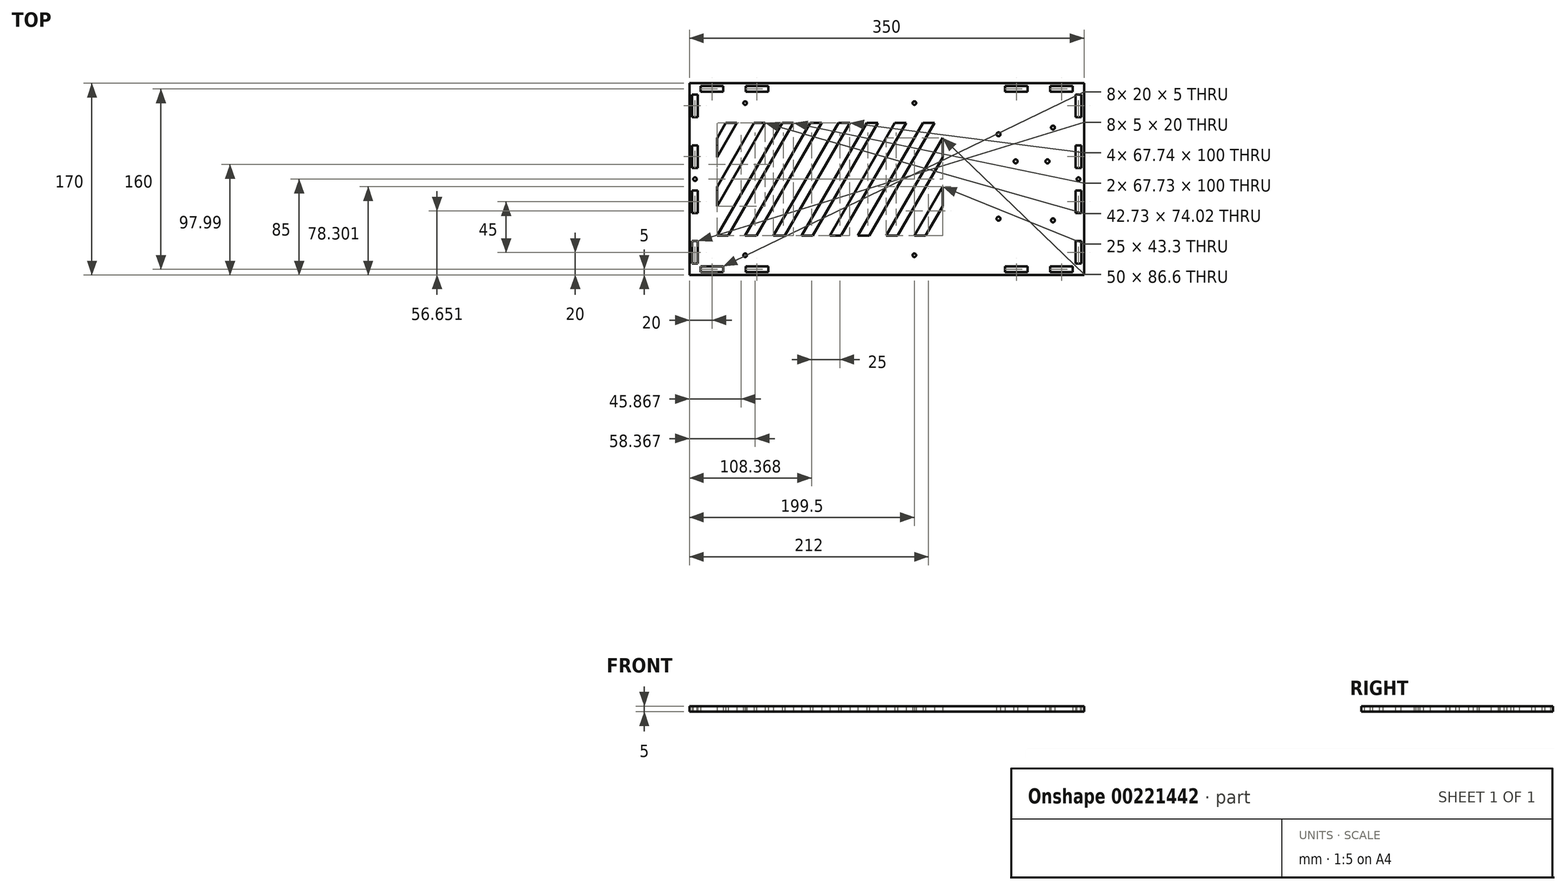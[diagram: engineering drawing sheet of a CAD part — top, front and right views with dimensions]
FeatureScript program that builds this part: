
annotation { "Feature Type Name" : "Feature", "Feature Type Description" : "" }
export const myFeature = defineFeature(function(context is Context, id is Id, definition is map)
    precondition{}
    {
        {
            assignVariable(context, id + "F0", {"name" : "thickness", "anyValue" : 5 * mm});
        }
        {
            var Q0;
            Q0=qCreatedBy(makeId("Top.planeOp"),FACE);
            var sketch = newSketch(context, id + "F1", { "sketchPlane" : qUnion([Q0])});
            skLineSegment(sketch, "E0.bottom", {"start": v(0, 0) * mm, "end": v(350, 0) * mm});
            skLineSegment(sketch, "E0.top", {"start": v(0, 170) * mm, "end": v(350, 170) * mm});
            skLineSegment(sketch, "E0.left", {"start": v(0, 0) * mm, "end": v(0, 170) * mm});
            skLineSegment(sketch, "E0.right", {"start": v(350, 0) * mm, "end": v(350, 170) * mm});
            skLineSegment(sketch, "E1.0", {"start": v(10, 160) * mm, "end": v(340, 160) * mm, "construction": true});
            skLineSegment(sketch, "E1.1", {"start": v(10, 10) * mm, "end": v(10, 160) * mm, "construction": true});
            skLineSegment(sketch, "E1.2", {"start": v(10, 10) * mm, "end": v(340, 10) * mm, "construction": true});
            skLineSegment(sketch, "E1.3", {"start": v(340, 10) * mm, "end": v(340, 160) * mm, "construction": true});
            skLineSegment(sketch, "E2.bottom", {"start": v(325, 34.25) * mm, "end": v(325, 135.75) * mm, "construction": true});
            skLineSegment(sketch, "E2.top", {"start": v(271.5, 34.25) * mm, "end": v(271.5, 135.75) * mm, "construction": true});
            skLineSegment(sketch, "E2.left", {"start": v(325, 34.25) * mm, "end": v(271.5, 34.25) * mm, "construction": true});
            skLineSegment(sketch, "E2.right", {"start": v(325, 135.75) * mm, "end": v(271.5, 135.75) * mm, "construction": true});
            skCircle(sketch, "E3", {"center": v(322.4, 48.45) * mm, "radius": 1.75 * mm});
            skCircle(sketch, "E4", {"center": v(274.1, 49.85) * mm, "radius": 1.75 * mm});
            skCircle(sketch, "E5", {"center": v(289.3, 100.75) * mm, "radius": 1.75 * mm});
            skCircle(sketch, "E6", {"center": v(317.5, 100.75) * mm, "radius": 1.75 * mm});
            skCircle(sketch, "E7", {"center": v(274.1, 124.75) * mm, "radius": 1.75 * mm});
            skCircle(sketch, "E8", {"center": v(322.4, 130.75) * mm, "radius": 1.75 * mm});
            skPoint(sketch, "E9", {"position": v(298.25, 34.25) * mm});
            skPoint(sketch, "E10", {"position": v(325, 85) * mm});
            skPoint(sketch, "E11", {"position": v(340, 85) * mm});
            skLineSegment(sketch, "E12.bottom", {"start": v(17, 142.5) * mm, "end": v(232, 142.5) * mm, "construction": true});
            skLineSegment(sketch, "E12.top", {"start": v(17, 27.5) * mm, "end": v(232, 27.5) * mm, "construction": true});
            skLineSegment(sketch, "E12.left", {"start": v(17, 142.5) * mm, "end": v(17, 27.5) * mm, "construction": true});
            skLineSegment(sketch, "E12.right", {"start": v(232, 142.5) * mm, "end": v(232, 27.5) * mm, "construction": true});
            skPoint(sketch, "E13", {"position": v(232, 85) * mm});
            skCircle(sketch, "E14", {"center": v(199.5, 152.5) * mm, "radius": 1.6 * mm});
            skCircle(sketch, "E15", {"center": v(199.5, 17.5) * mm, "radius": 1.6 * mm});
            skLineSegment(sketch, "E16", {"start": v(199.5, 152.5) * mm, "end": v(199.5, 17.5) * mm, "construction": true});
            skPoint(sketch, "E17", {"position": v(199.5, 85) * mm});
            skCircle(sketch, "E18", {"center": v(49.5, 152.5) * mm, "radius": 1.6 * mm});
            skCircle(sketch, "E19", {"center": v(49.5, 17.5) * mm, "radius": 1.6 * mm});
            skLineSegment(sketch, "E20", {"start": v(49.5, 152.5) * mm, "end": v(49.5, 17.5) * mm, "construction": true});
            skPoint(sketch, "E21", {"position": v(49.5, 85) * mm});
            skLineSegment(sketch, "E22.bottom", {"start": v(10, 7.5) * mm, "end": v(30, 7.5) * mm});
            skLineSegment(sketch, "E22.top", {"start": v(10, 2.5) * mm, "end": v(30, 2.5) * mm});
            skLineSegment(sketch, "E22.left", {"start": v(10, 7.5) * mm, "end": v(10, 2.5) * mm});
            skLineSegment(sketch, "E22.right", {"start": v(30, 7.5) * mm, "end": v(30, 2.5) * mm});
            skPoint(sketch, "E22.middle", {"position": v(20, 5) * mm});
            skLineSegment(sketch, "E23", {"start": v(10, 10) * mm, "end": v(10, 0) * mm, "construction": true});
            skPoint(sketch, "E24", {"position": v(10, 5) * mm});
            skLineSegment(sketch, "E25.bottom", {"start": v(50, 7.5) * mm, "end": v(70, 7.5) * mm});
            skLineSegment(sketch, "E25.top", {"start": v(50, 2.5) * mm, "end": v(70, 2.5) * mm});
            skLineSegment(sketch, "E25.left", {"start": v(50, 7.5) * mm, "end": v(50, 2.5) * mm});
            skLineSegment(sketch, "E25.right", {"start": v(70, 7.5) * mm, "end": v(70, 2.5) * mm});
            skPoint(sketch, "E25.middle", {"position": v(60, 5) * mm});
            skLineSegment(sketch, "E26", {"start": v(175, 10) * mm, "end": v(175, 0) * mm, "construction": true});
            skLineSegment(sketch, "E27.MirrorCS", {"start": v(300, 2.5) * mm, "end": v(280, 2.5) * mm});
            skLineSegment(sketch, "E28.MirrorCS", {"start": v(320, 7.5) * mm, "end": v(320, 2.5) * mm});
            skPoint(sketch, "E29.MirrorP", {"position": v(330, 5) * mm});
            skLineSegment(sketch, "E30.MirrorCS", {"start": v(300, 7.5) * mm, "end": v(280, 7.5) * mm});
            skLineSegment(sketch, "E31.MirrorCS", {"start": v(340, 2.5) * mm, "end": v(320, 2.5) * mm});
            skLineSegment(sketch, "E32.MirrorCS", {"start": v(280, 7.5) * mm, "end": v(280, 2.5) * mm});
            skPoint(sketch, "E33.MirrorP", {"position": v(290, 5) * mm});
            skLineSegment(sketch, "E34.MirrorCS", {"start": v(300, 7.5) * mm, "end": v(300, 2.5) * mm});
            skLineSegment(sketch, "E35.MirrorCS", {"start": v(340, 7.5) * mm, "end": v(340, 2.5) * mm});
            skLineSegment(sketch, "E36.MirrorCS", {"start": v(340, 7.5) * mm, "end": v(320, 7.5) * mm});
            skLineSegment(sketch, "E37", {"start": v(0, 85) * mm, "end": v(350, 85) * mm, "construction": true});
            skLineSegment(sketch, "E38.MirrorCS", {"start": v(30, 162.5) * mm, "end": v(30, 167.5) * mm});
            skPoint(sketch, "E39.MirrorP", {"position": v(20, 165) * mm});
            skLineSegment(sketch, "E40.MirrorCS", {"start": v(10, 167.5) * mm, "end": v(30, 167.5) * mm});
            skLineSegment(sketch, "E41.MirrorCS", {"start": v(10, 162.5) * mm, "end": v(10, 167.5) * mm});
            skPoint(sketch, "E42.MirrorP", {"position": v(10, 165) * mm});
            skLineSegment(sketch, "E43.MirrorCS", {"start": v(10, 162.5) * mm, "end": v(30, 162.5) * mm});
            skLineSegment(sketch, "E44.MirrorCS", {"start": v(50, 167.5) * mm, "end": v(70, 167.5) * mm});
            skLineSegment(sketch, "E45.MirrorCS", {"start": v(50, 162.5) * mm, "end": v(50, 167.5) * mm});
            skLineSegment(sketch, "E46.MirrorCS", {"start": v(50, 162.5) * mm, "end": v(70, 162.5) * mm});
            skPoint(sketch, "E47.MirrorP", {"position": v(60, 165) * mm});
            skLineSegment(sketch, "E48.MirrorCS", {"start": v(70, 162.5) * mm, "end": v(70, 167.5) * mm});
            skLineSegment(sketch, "E49.MirrorCS", {"start": v(300, 167.5) * mm, "end": v(280, 167.5) * mm});
            skLineSegment(sketch, "E50.MirrorCS", {"start": v(280, 162.5) * mm, "end": v(280, 167.5) * mm});
            skLineSegment(sketch, "E51.MirrorCS", {"start": v(340, 167.5) * mm, "end": v(320, 167.5) * mm});
            skPoint(sketch, "E52.MirrorP", {"position": v(290, 165) * mm});
            skPoint(sketch, "E53.MirrorP", {"position": v(330, 165) * mm});
            skLineSegment(sketch, "E54.MirrorCS", {"start": v(340, 162.5) * mm, "end": v(320, 162.5) * mm});
            skLineSegment(sketch, "E55.MirrorCS", {"start": v(320, 162.5) * mm, "end": v(320, 167.5) * mm});
            skLineSegment(sketch, "E56.MirrorCS", {"start": v(300, 162.5) * mm, "end": v(300, 167.5) * mm});
            skLineSegment(sketch, "E57.MirrorCS", {"start": v(300, 162.5) * mm, "end": v(280, 162.5) * mm});
            skLineSegment(sketch, "E58.MirrorCS", {"start": v(340, 162.5) * mm, "end": v(340, 167.5) * mm});
            skLineSegment(sketch, "E59.bottom", {"start": v(7.5, 30) * mm, "end": v(2.5, 30) * mm});
            skLineSegment(sketch, "E59.top", {"start": v(7.5, 10) * mm, "end": v(2.5, 10) * mm});
            skLineSegment(sketch, "E59.left", {"start": v(7.5, 30) * mm, "end": v(7.5, 10) * mm});
            skLineSegment(sketch, "E59.right", {"start": v(2.5, 30) * mm, "end": v(2.5, 10) * mm});
            skPoint(sketch, "E59.middle", {"position": v(5, 20) * mm});
            skLineSegment(sketch, "E60", {"start": v(10, 10) * mm, "end": v(0, 10) * mm, "construction": true});
            skPoint(sketch, "E61", {"position": v(5, 10) * mm});
            skLineSegment(sketch, "E62.bottom", {"start": v(7.5, 75) * mm, "end": v(2.5, 75) * mm});
            skLineSegment(sketch, "E62.top", {"start": v(7.5, 55) * mm, "end": v(2.5, 55) * mm});
            skLineSegment(sketch, "E62.left", {"start": v(7.5, 75) * mm, "end": v(7.5, 55) * mm});
            skLineSegment(sketch, "E62.right", {"start": v(2.5, 75) * mm, "end": v(2.5, 55) * mm});
            skPoint(sketch, "E62.middle", {"position": v(5, 65) * mm});
            skCircle(sketch, "E63", {"center": v(5, 85) * mm, "radius": 1.6 * mm});
            skPoint(sketch, "E63.centerSnap0", {"position": v(5, 75) * mm});
            skLineSegment(sketch, "E64.MirrorCS", {"start": v(7.5, 95) * mm, "end": v(2.5, 95) * mm});
            skPoint(sketch, "E65.MirrorP", {"position": v(5, 105) * mm});
            skLineSegment(sketch, "E66.MirrorCS", {"start": v(7.5, 95) * mm, "end": v(7.5, 115) * mm});
            skLineSegment(sketch, "E67.MirrorCS", {"start": v(7.5, 115) * mm, "end": v(2.5, 115) * mm});
            skLineSegment(sketch, "E68.MirrorCS", {"start": v(2.5, 95) * mm, "end": v(2.5, 115) * mm});
            skLineSegment(sketch, "E69.MirrorCS", {"start": v(7.5, 160) * mm, "end": v(2.5, 160) * mm});
            skLineSegment(sketch, "E70.MirrorCS", {"start": v(2.5, 140) * mm, "end": v(2.5, 160) * mm});
            skLineSegment(sketch, "E71.MirrorCS", {"start": v(7.5, 140) * mm, "end": v(7.5, 160) * mm});
            skLineSegment(sketch, "E72.MirrorCS", {"start": v(7.5, 140) * mm, "end": v(2.5, 140) * mm});
            skPoint(sketch, "E73.MirrorP", {"position": v(5, 150) * mm});
            skLineSegment(sketch, "E74.MirrorCS", {"start": v(342.5, 75) * mm, "end": v(347.5, 75) * mm});
            skCircle(sketch, "E75.MirrorC", {"center": v(345, 85) * mm, "radius": 1.6 * mm});
            skLineSegment(sketch, "E76.MirrorCS", {"start": v(342.5, 10) * mm, "end": v(347.5, 10) * mm});
            skLineSegment(sketch, "E77.MirrorCS", {"start": v(347.5, 30) * mm, "end": v(347.5, 10) * mm});
            skLineSegment(sketch, "E78.MirrorCS", {"start": v(342.5, 95) * mm, "end": v(347.5, 95) * mm});
            skLineSegment(sketch, "E79.MirrorCS", {"start": v(342.5, 95) * mm, "end": v(342.5, 115) * mm});
            skPoint(sketch, "E80.MirrorP", {"position": v(345, 65) * mm});
            skPoint(sketch, "E81.MirrorP", {"position": v(345, 75) * mm});
            skLineSegment(sketch, "E82.MirrorCS", {"start": v(342.5, 115) * mm, "end": v(347.5, 115) * mm});
            skLineSegment(sketch, "E83.MirrorCS", {"start": v(342.5, 160) * mm, "end": v(347.5, 160) * mm});
            skLineSegment(sketch, "E84.MirrorCS", {"start": v(342.5, 30) * mm, "end": v(342.5, 10) * mm});
            skPoint(sketch, "E85.MirrorP", {"position": v(345, 105) * mm});
            skLineSegment(sketch, "E86.MirrorCS", {"start": v(342.5, 75) * mm, "end": v(342.5, 55) * mm});
            skLineSegment(sketch, "E87.MirrorCS", {"start": v(342.5, 30) * mm, "end": v(347.5, 30) * mm});
            skLineSegment(sketch, "E88.MirrorCS", {"start": v(342.5, 140) * mm, "end": v(342.5, 160) * mm});
            skPoint(sketch, "E89.MirrorP", {"position": v(345, 20) * mm});
            skLineSegment(sketch, "E90.MirrorCS", {"start": v(347.5, 75) * mm, "end": v(347.5, 55) * mm});
            skLineSegment(sketch, "E91.MirrorCS", {"start": v(342.5, 55) * mm, "end": v(347.5, 55) * mm});
            skLineSegment(sketch, "E92.MirrorCS", {"start": v(347.5, 140) * mm, "end": v(347.5, 160) * mm});
            skPoint(sketch, "E93.MirrorP", {"position": v(345, 150) * mm});
            skLineSegment(sketch, "E94.MirrorCS", {"start": v(347.5, 95) * mm, "end": v(347.5, 115) * mm});
            skPoint(sketch, "E95.MirrorP", {"position": v(345, 10) * mm});
            skLineSegment(sketch, "E96.MirrorCS", {"start": v(342.5, 140) * mm, "end": v(347.5, 140) * mm});
            skLineSegment(sketch, "E97.bottom", {"start": v(24.5, 35) * mm, "end": v(224.5, 35) * mm, "construction": true});
            skLineSegment(sketch, "E97.top", {"start": v(24.5, 135) * mm, "end": v(224.5, 135) * mm, "construction": true});
            skLineSegment(sketch, "E97.left", {"start": v(24.5, 35) * mm, "end": v(24.5, 135) * mm, "construction": true});
            skLineSegment(sketch, "E97.right", {"start": v(224.5, 35) * mm, "end": v(224.5, 135) * mm, "construction": true});
            skPoint(sketch, "E98", {"position": v(24.5, 85) * mm});
            skPoint(sketch, "E99", {"position": v(124.5, 135) * mm});
            skPoint(sketch, "E100", {"position": v(124.5, 142.5) * mm});
            skLineSegment(sketch, "E101", {"start": v(24.5, 35) * mm, "end": v(82.24, 135) * mm});
            skLineSegment(sketch, "E102", {"start": v(82.24, 135) * mm, "end": v(92.24, 135) * mm});
            skLineSegment(sketch, "E103", {"start": v(92.24, 135) * mm, "end": v(34.5, 35) * mm});
            skLineSegment(sketch, "E104", {"start": v(34.5, 35) * mm, "end": v(24.5, 35) * mm});
            skLineSegment(sketch, "E105.1.0.0", {"start": v(49.5, 35) * mm, "end": v(107.24, 135) * mm});
            skLineSegment(sketch, "E105.1.0.1", {"start": v(117.24, 135) * mm, "end": v(59.5, 35) * mm});
            skLineSegment(sketch, "E105.1.0.2", {"start": v(107.24, 135) * mm, "end": v(117.24, 135) * mm});
            skLineSegment(sketch, "E105.1.0.3", {"start": v(59.5, 35) * mm, "end": v(49.5, 35) * mm});
            skLineSegment(sketch, "E105.2.0.0", {"start": v(74.5, 35) * mm, "end": v(132.24, 135) * mm});
            skLineSegment(sketch, "E105.2.0.1", {"start": v(142.24, 135) * mm, "end": v(84.5, 35) * mm});
            skLineSegment(sketch, "E105.2.0.2", {"start": v(132.24, 135) * mm, "end": v(142.24, 135) * mm});
            skLineSegment(sketch, "E105.2.0.3", {"start": v(84.5, 35) * mm, "end": v(74.5, 35) * mm});
            skLineSegment(sketch, "E105.3.0.0", {"start": v(99.5, 35) * mm, "end": v(157.24, 135) * mm});
            skLineSegment(sketch, "E105.3.0.1", {"start": v(167.24, 135) * mm, "end": v(109.5, 35) * mm});
            skLineSegment(sketch, "E105.3.0.2", {"start": v(157.24, 135) * mm, "end": v(167.24, 135) * mm});
            skLineSegment(sketch, "E105.3.0.3", {"start": v(109.5, 35) * mm, "end": v(99.5, 35) * mm});
            skLineSegment(sketch, "E105.4.0.0", {"start": v(124.5, 35) * mm, "end": v(182.24, 135) * mm});
            skLineSegment(sketch, "E105.4.0.1", {"start": v(192.24, 135) * mm, "end": v(134.5, 35) * mm});
            skLineSegment(sketch, "E105.4.0.2", {"start": v(182.24, 135) * mm, "end": v(192.24, 135) * mm});
            skLineSegment(sketch, "E105.4.0.3", {"start": v(134.5, 35) * mm, "end": v(124.5, 35) * mm});
            skLineSegment(sketch, "E105.5.0.0", {"start": v(149.5, 35) * mm, "end": v(207.24, 135) * mm});
            skLineSegment(sketch, "E105.5.0.1", {"start": v(217.24, 135) * mm, "end": v(159.5, 35) * mm});
            skLineSegment(sketch, "E105.5.0.2", {"start": v(207.24, 135) * mm, "end": v(217.24, 135) * mm});
            skLineSegment(sketch, "E105.5.0.3", {"start": v(159.5, 35) * mm, "end": v(149.5, 35) * mm});
            skLineSegment(sketch, "E105.6.0.0", {"start": v(174.5, 35) * mm, "end": v(224.5, 121.6) * mm});
            skLineSegment(sketch, "E105.6.0.3", {"start": v(184.5, 35) * mm, "end": v(174.5, 35) * mm});
            skLineSegment(sketch, "E105.7.0.0", {"start": v(199.5, 35) * mm, "end": v(224.5, 78.3) * mm});
            skLineSegment(sketch, "E105.7.0.3", {"start": v(209.5, 35) * mm, "end": v(199.5, 35) * mm});
            skLineSegment(sketch, "E105.direction1", {"start": v(24.5, 35) * mm, "end": v(49.5, 35) * mm, "construction": true});
            skLineSegment(sketch, "E106", {"start": v(224.5, 121.6) * mm, "end": v(224.5, 104.1) * mm});
            skLineSegment(sketch, "E107", {"start": v(224.5, 78.3) * mm, "end": v(224.5, 60.91) * mm});
            skLineSegment(sketch, "E108.trimOffspring", {"start": v(224.5, 104.1) * mm, "end": v(184.5, 35) * mm});
            skLineSegment(sketch, "E109.trimOffspring", {"start": v(224.5, 60.91) * mm, "end": v(209.5, 35) * mm});
            skLineSegment(sketch, "E110.1.0.1", {"start": v(67.24, 135) * mm, "end": v(24.5, 60.98) * mm});
            skLineSegment(sketch, "E110.1.0.2", {"start": v(57.24, 135) * mm, "end": v(67.24, 135) * mm});
            skLineSegment(sketch, "E110.1.0.3", {"start": v(9.5, 35) * mm, "end": v(-0.5, 35) * mm});
            skLineSegment(sketch, "E110.2.0.1", {"start": v(42.24, 135) * mm, "end": v(24.5, 104.28) * mm});
            skLineSegment(sketch, "E110.2.0.2", {"start": v(32.24, 135) * mm, "end": v(42.24, 135) * mm});
            skLineSegment(sketch, "E110.direction1", {"start": v(24.5, 35) * mm, "end": v(-0.5, 35) * mm, "construction": true});
            skLineSegment(sketch, "E111.trimOffspring", {"start": v(24.5, 121.37) * mm, "end": v(32.24, 135) * mm});
            skLineSegment(sketch, "E112.trimOffspring", {"start": v(24.5, 78.19) * mm, "end": v(57.24, 135) * mm});
            skLineSegment(sketch, "E113", {"start": v(24.5, 121.37) * mm, "end": v(24.5, 104.28) * mm});
            skLineSegment(sketch, "E114", {"start": v(24.5, 78.19) * mm, "end": v(24.5, 60.98) * mm});
            skSolve(sketch);
        }
        {
            var Q0;
            Q0 = qSketchRegion(id + "F1", true);
            extrude(context, id + "F2", {"entities" : qUnion([Q0]), "depth" : getVariable(context, 'thickness')});
        }
    });
